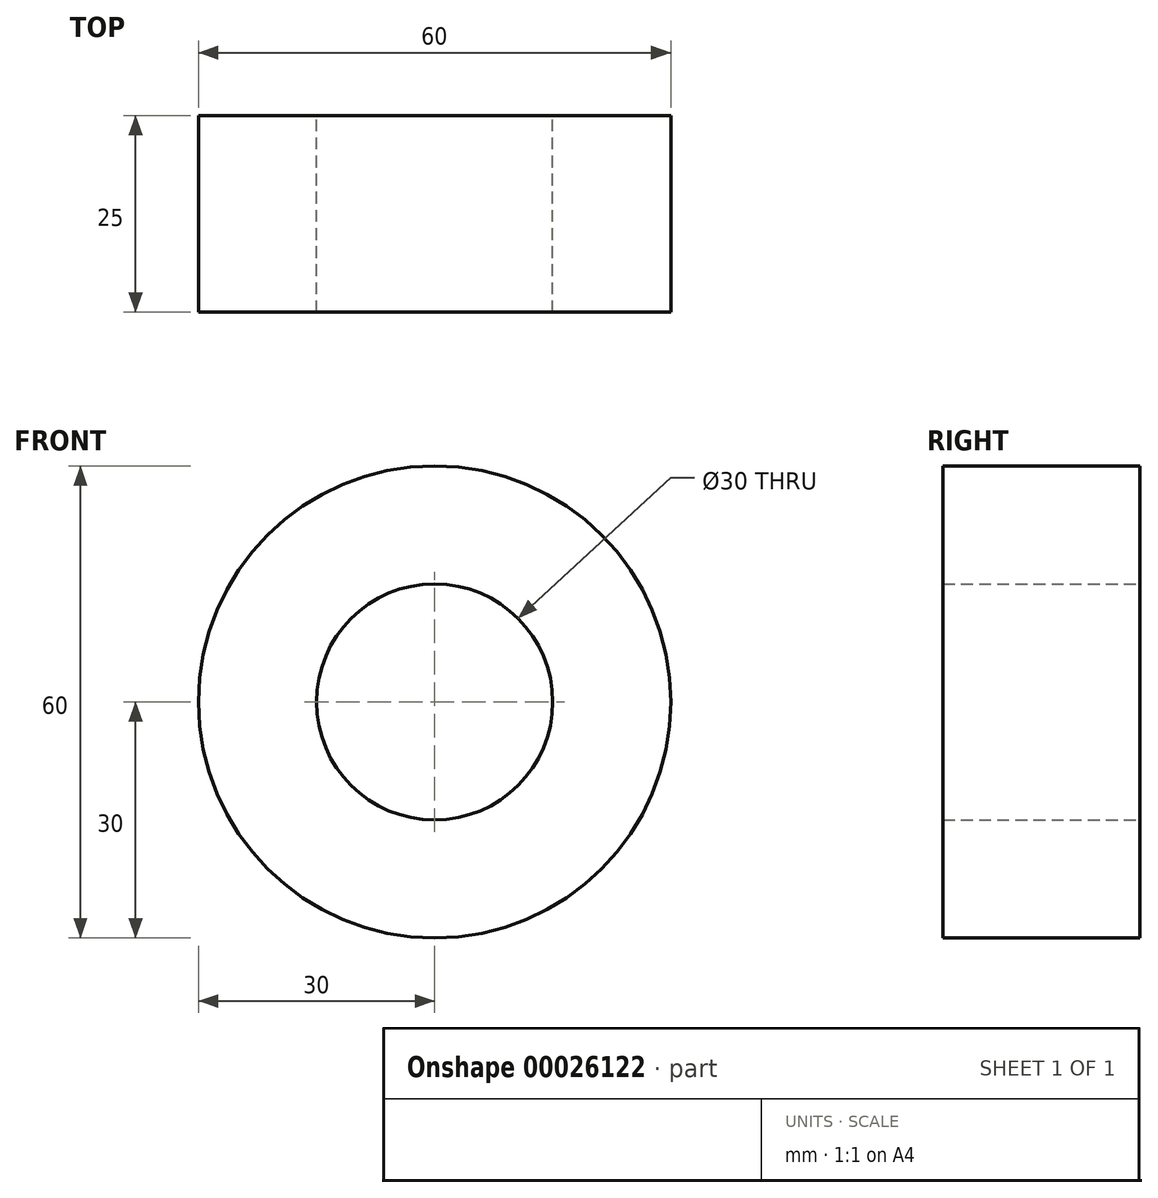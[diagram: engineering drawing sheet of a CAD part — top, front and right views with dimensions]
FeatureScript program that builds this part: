
annotation { "Feature Type Name" : "Feature", "Feature Type Description" : "" }
export const myFeature = defineFeature(function(context is Context, id is Id, definition is map)
    precondition{}
    {
        {
            var Q0;
            Q0=qCreatedBy(makeId("Front.planeOp"),FACE);
            var sketch = newSketch(context, id + "F0", { "sketchPlane" : qUnion([Q0])});
            skCircle(sketch, "E0", {"center": v(0, 0) * mm, "radius": 30 * mm});
            skCircle(sketch, "E1", {"center": v(0, 0) * mm, "radius": 15 * mm});
            skSolve(sketch);
        }
        {
            var Q0;
            Q0=makeQuery(id+"F0.imprint","IMPRINT",FACE,{"disambiguationData":[TD([[makeQuery(id+"F0.imprint","IMPRINT",EDGE,{"derivedFrom":sQuery(id+"F0.wireOp",EDGE,"E0")}),1.0]])]});
            extrude(context, id + "F1", {"entities" : qUnion([Q0]), "depth" : 25 * mm});
        }
    });
